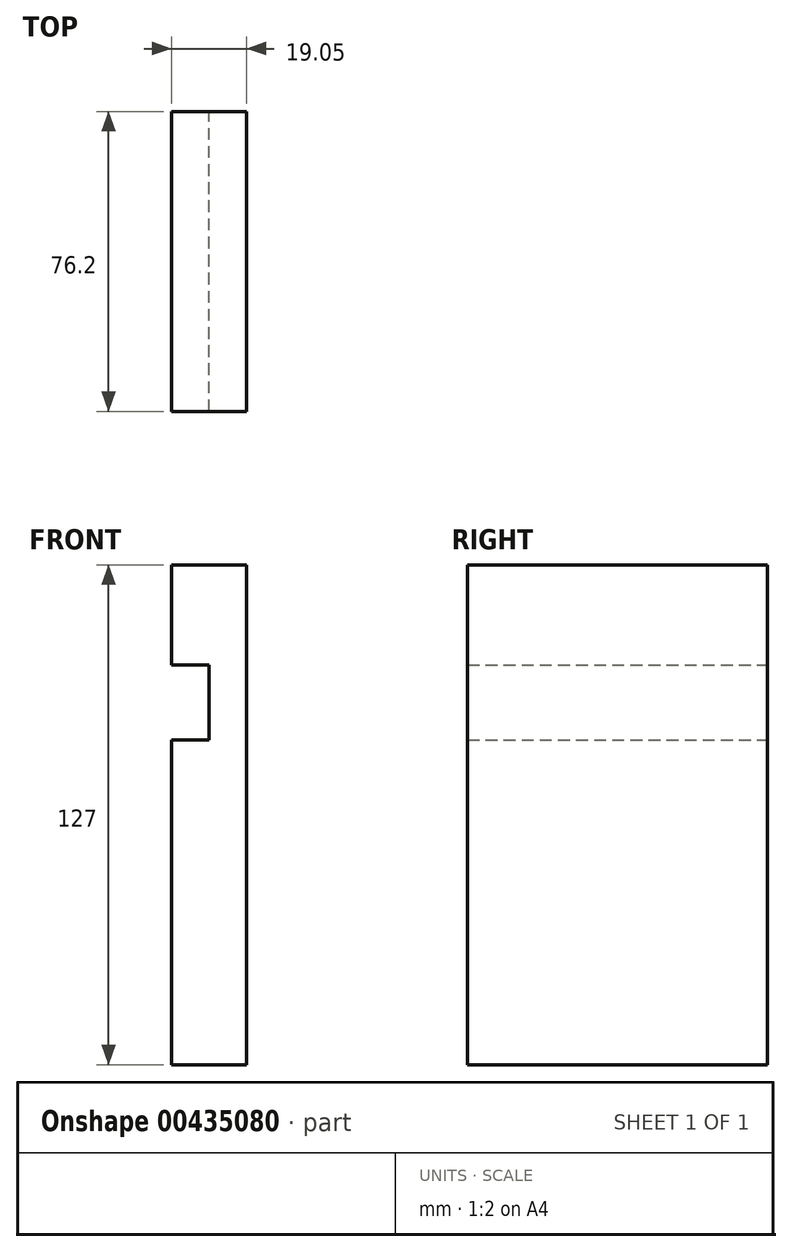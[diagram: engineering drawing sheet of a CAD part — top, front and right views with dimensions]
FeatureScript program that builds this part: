
annotation { "Feature Type Name" : "Feature", "Feature Type Description" : "" }
export const myFeature = defineFeature(function(context is Context, id is Id, definition is map)
    precondition{}
    {
        {
            var Q0;
            Q0=qCreatedBy(makeId("Front.planeOp"),FACE);
            var sketch = newSketch(context, id + "F0", { "sketchPlane" : qUnion([Q0])});
            skLineSegment(sketch, "E0", {"start": v(27, -72.5) * mm, "end": v(27, 54.5) * mm});
            skLineSegment(sketch, "E1", {"start": v(27, 54.5) * mm, "end": v(7.96, 54.5) * mm});
            skLineSegment(sketch, "E2", {"start": v(7.96, 54.5) * mm, "end": v(7.96, 29.1) * mm});
            skLineSegment(sketch, "E3", {"start": v(7.96, 29.1) * mm, "end": v(17.48, 29.1) * mm});
            skLineSegment(sketch, "E4", {"start": v(17.48, 29.1) * mm, "end": v(17.48, 10.04) * mm});
            skLineSegment(sketch, "E5", {"start": v(17.48, 10.04) * mm, "end": v(7.96, 10.04) * mm});
            skLineSegment(sketch, "E6", {"start": v(7.96, 10.04) * mm, "end": v(7.96, -72.06) * mm});
            skLineSegment(sketch, "E7", {"start": v(27, -72.5) * mm, "end": v(7.96, -72.5) * mm});
            skLineSegment(sketch, "E8", {"start": v(7.96, -72.5) * mm, "end": v(7.96, -67.5) * mm});
            skSolve(sketch);
        }
        {
            var Q0;
            Q0 = qSketchRegion(id + "F0", true);
            extrude(context, id + "F1", {"entities" : qUnion([Q0]), "depth" : 76.2 * mm});
        }
    });
